# Revit family: HUNTER_ICD-200-Decoder
name_source: partatom
category: Electrical Fixtures
revit_build: Autodesk Revit 2017 (Build: 20160225_1515(x64)
units: mm (PartAtom-declared; Revit-internal decimal feet)

## family parameters
Always vertical = Yes
Cut with Voids When Loaded = No
Maintain Annotation Orientation = No
OmniClass Number = 23.35.41.13
Part Type = Normal
Room Calculation Point = No
Round Connector Dimension = Use Diameter
Shared = Yes
Work Plane-Based = Yes

## types (1)
- ICD-200
    Assembly Code = D5030.50
    Default Elevation = 1219 mm
    Description = 2-station decoder with surge suppression
    Height = 250 mm
    ICD Depth = 13 mm
    ICD Height = 92 mm  [stored 0.301837 ft]
    ICD Width = 38 mm  [stored 0.124672 ft]
    Input Voltage = 24 V
    Keynote = 26 09 00
    Manufacturer = Hunter® Industries
    Model = 2-station decoder with surge suppression and ground wire
    Type Comments = ICD-200
    URL = https://www.hunterindustries.com

note: [stored X ft] marks values corroborated as IEEE doubles in the binary element streams (Revit-internal decimal feet)

## geometry (parser evidence)
native form markers: Sweep x6
no freeform markers — native parametric forms only
